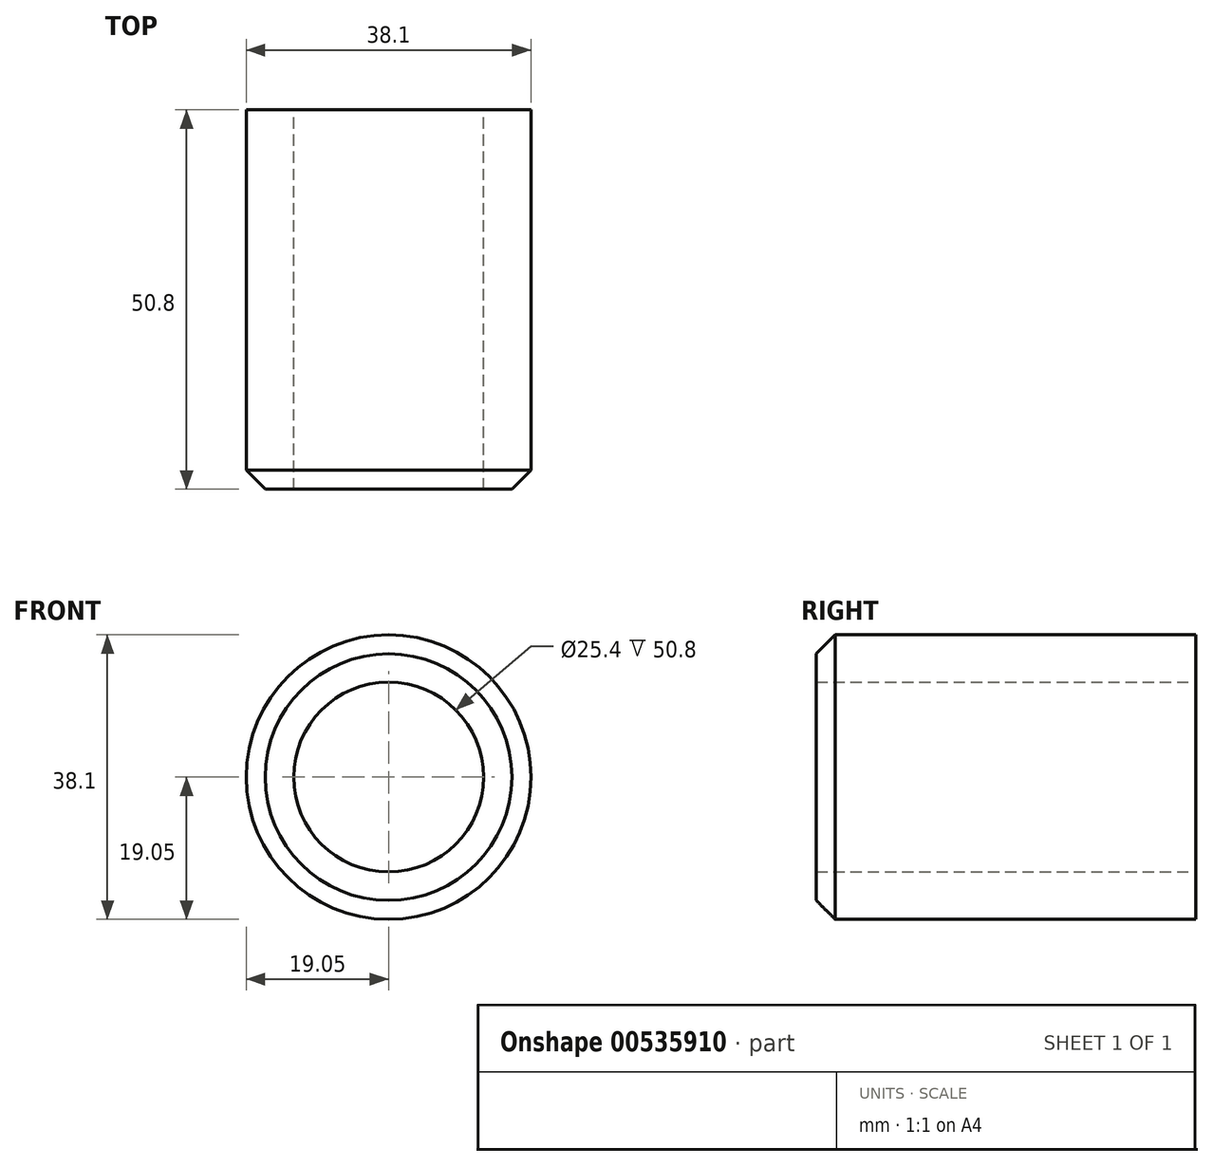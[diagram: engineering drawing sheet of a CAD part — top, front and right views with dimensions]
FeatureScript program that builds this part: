
annotation { "Feature Type Name" : "Feature", "Feature Type Description" : "" }
export const myFeature = defineFeature(function(context is Context, id is Id, definition is map)
    precondition{}
    {
        {
            var Q0;
            Q0=qCreatedBy(makeId("Front.planeOp"),FACE);
            var sketch = newSketch(context, id + "F0", { "sketchPlane" : qUnion([Q0])});
            skCircle(sketch, "E0", {"center": v(0, 0) * mm, "radius": 12.7 * mm});
            skCircle(sketch, "E1", {"center": v(0, 0) * mm, "radius": 19.05 * mm});
            skCircle(sketch, "E2", {"center": v(0, 0) * mm, "radius": 25.4 * mm});
            skSolve(sketch);
        }
        {
            var Q0;
            Q0=makeQuery(id+"F0.imprint","IMPRINT",FACE,{"disambiguationData":[TD([[makeQuery(id+"F0.imprint","IMPRINT",EDGE,{"derivedFrom":sQuery(id+"F0.wireOp",EDGE,"E0")}),-1.0]])]});
            extrude(context, id + "F1", {"entities" : qUnion([Q0]), "depth" : 50.8 * mm, "offsetDistance" : 25.4 * mm});
        }
        {
            var Q0;
            Q0=makeQuery(id+"F1.opExtrude","CAP_EDGE",EDGE,{"disambiguationData":[OSD([sQuery(id+"F0.wireOp",EDGE,"E1")])],"isStart":false});
            chamfer(context, id + "F2", {"entities" : qUnion([Q0]), "width" : 2.54 * mm, "tangentPropagation" : true});
        }
    });
